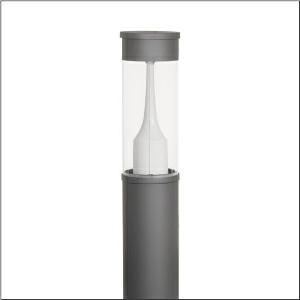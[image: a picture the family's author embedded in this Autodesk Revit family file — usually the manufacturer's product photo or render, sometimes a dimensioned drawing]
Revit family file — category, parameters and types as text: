
# Revit family: city-light_400_iq___p1_0a_5xa5305ff14h_0bc5
name_source: partatom
category: Lighting Fixtures
units: mm (PartAtom-declared; Revit-internal decimal feet)

## family parameters
Cut with Voids When Loaded = No
Host = Face
Light Source = No
Part Type = Normal
Room Calculation Point = No
Round Connector Dimension = Use Diameter
Shared = No

## types (1)
- --- (1 x LED, 1510 lm, 10.5 W, 3000K)
    Apparent Load = 11 VA
    CIE Flux Codes = 32 61 90 93 100
    Color Rendering = 70
    Color Temperature = 3000K
    Default Elevation = 1800 mm
    Description = City-Light 400 iQ, light pillar, Module 540 iQ-SR, primary light control with 3 zone facetted reflector, of plastic, silver coated, highly specular, structured, primary optical cover: cover, of PMMA, transparent, light distribution: P1.0a, primary light characteristic: strongly asymmetric, LED, High Power LED, rated luminous flux: 1.510lm, luminous efficacy: 144lm/W, light colour: 730, colour temperature: 3000K, control gear: iQ Street-Remote, control: Auto-Match, Temp-Guard, Lumen-Switch, Night-Set, Smart-Wire, Light-Fading, Desk-Remote (wireless, voltage-free reading and setting of iQ features in the workshop via application-optimized NFC function/RFID function), optimised constant luminous flux control (CLO 2.0), Street-Remote, pre-setting: logarithmic dimming characteristic, with terminal, 6-pole, max. 2.5mm², mains connection: 230..240V, AC, 50/60Hz, start of lifetime: 11W, end of service life: 11W, reduction: 5W, luminaire housing, cylindrical, of extruded aluminium section, coated, Siteco® metallic grey (DB 702S), length: 4.694mm, diameter: 200mm, Module 540 iQ-SR, traffic white (RAL 9016), equipment: standard, protection rating (complete): IP65, insulation class (complete): insulation class II (safety insulation), certification: CE, ENEC, VDE, packaging unit: 1 piece

Light Distribution: P1.0a
    Height = 500 mm
    Lamp = 1 x LED
    Lamp Light Flux = 1510 lm
    Lamp Power = 10.5 W
    Lamp count = 1
    Length = 200 mm  [stored 0.656168 ft]
    Luminous efficacy = 144 lm/W
    Manufacturer = Siteco
    ModVariant = No
    Model = 5XA5305FF14H
    Mounting Place = Floor
    Mounting Type = Freestanding
    Number of Poles = 1
    OnlyDefault = Yes
    Power Factor = 1
    Product Name = City-Light 400 iQ | P1.0a
    Product group = light pillar
    ProductGroupID = 1301
    Protection Class = Protection class II
    Protection Degree = IP 65
    RLX_Detail_Level = 1
    RLX_Emergency_Light_Flux = 0 lm
    RLX_Emergency_Type = 0
    RLX_Emergency_Type_DB = No
    RlxData = <blob elided: 75309 chars, md5=d4bd3ada>
    Socket = socket
    Standby Power = 0 W
    System Light Flux = 1510 lm
    System Power = 11 W
    Type Comments = factory setting: luminous flux: 100 % | dim-lin: 254 | 419 mA
    Type Image = l_1006914.jpg
    URL = http://relux.com
    VarID = @adj_160433
    Voltage = 0 V
    Weight = 0.00 kg
    Width = 0 mm  [stored 0 ft]

note: [stored X ft] marks values corroborated as IEEE doubles in the binary element streams (Revit-internal decimal feet)

## geometry (parser evidence)
native form markers: Blend x4, Sweep x11
no freeform markers — native parametric forms only
